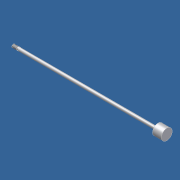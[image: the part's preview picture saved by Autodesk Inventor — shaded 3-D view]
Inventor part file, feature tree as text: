
AUTODESK INVENTOR PART (.ipt)
format: ipt  version: 2012 (Build 160160000, 160)  size: 136,192 bytes
history: native  units: in
note: dims shown in document units (in); Inventor stores cm internally (conversion verified against a paired STEP export)
features: other x112, sketch x3, revolve x2, thread x1, extrude x1
ambient origin geometry x8: Origin, YZ Plane, XZ Plane, XY Plane, X Axis, Y Axis, Z Axis, Center Point
bodies: Solid1 (feature_tree)
feature tree (119):
  revolve  "Revolution1"  Angle=360.0deg
  revolve  "Revolution2"  [1 undecoded]
  thread  "Thread1"  [1 undecoded]
  extrude  "Extrusion1"  [1 undecoded]
  other  "rod_cp_XY"
  other  "rod_cp_YZ"
  other  "rod_cp_ZX"
  other  "rod_cp_X"
  other  "rod_cp_Y"
  other  "rod_cp_Z"
  other  "rod_cp_Center"
  other  "to_rod_clevis_XY"
  other  "to_rod_clevis_YZ"
  other  "to_rod_clevis_ZX"
  other  "to_rod_clevis_X"
  other  "to_rod_clevis_Y"
  other  "to_rod_clevis_Z"
  other  "to_rod_clevis_Center"
  other  "rl2_XY"
  other  "rl2_YZ"
  other  "rl2_ZX"
  other  "rl2_X"
  other  "rl2_Y"
  other  "rl2_Z"
  other  "rl2_Center"
  other  "rl1_XY"
  other  "rl1_YZ"
  other  "rl1_ZX"
  other  "rl1_X"
  other  "rl1_Y"
  other  "rl1_Z"
  other  "rl1_Center"
  other  "thd1_XY"
  other  "thd1_YZ"
  other  "thd1_ZX"
  other  "thd1_X"
  other  "thd1_Y"
  other  "thd1_Z"
  other  "thd1_Center"
  other  "thd2_XY"
  other  "thd2_YZ"
  other  "thd2_ZX"
  other  "thd2_X"
  other  "thd2_Y"
  other  "thd2_Z"
  other  "thd2_Center"
  other  "dia1_XY"
  other  "dia1_YZ"
  other  "dia1_ZX"
  other  "dia1_X"
  other  "dia1_Y"
  other  "dia1_Z"
  other  "dia1_Center"
  other  "dia2_XY"
  other  "dia2_YZ"
  other  "dia2_ZX"
  other  "dia2_X"
  other  "dia2_Y"
  other  "dia2_Z"
  other  "dia2_Center"
  other  "wf1_XY"
  other  "wf1_YZ"
  other  "wf1_ZX"
  other  "wf1_X"
  other  "wf1_Y"
  other  "wf1_Z"
  other  "wf1_Center"
  other  "wf2_XY"
  other  "wf2_YZ"
  other  "wf2_ZX"
  other  "wf2_X"
  other  "wf2_Y"
  other  "wf2_Z"
  other  "wf2_Center"
  other  "hh1_XY"
  other  "hh1_YZ"
  other  "hh1_ZX"
  other  "hh1_X"
  other  "hh1_Y"
  other  "hh1_Z"
  other  "hh1_Center"
  other  "hh2_XY"
  other  "hh2_YZ"
  other  "hh2_ZX"
  other  "hh2_X"
  other  "hh2_Y"
  other  "hh2_Z"
  other  "hh2_Center"
  other  "dia12_XY"
  other  "dia12_YZ"
  other  "dia12_ZX"
  other  "dia12_X"
  other  "dia12_Y"
  other  "dia12_Z"
  other  "dia12_Center"
  other  "dia22_XY"
  other  "dia22_YZ"
  other  "dia22_ZX"
  other  "dia22_X"
  other  "dia22_Y"
  other  "dia22_Z"
  other  "dia22_Center"
  other  "wfw1_XY"
  other  "wfw1_YZ"
  other  "wfw1_ZX"
  other  "wfw1_X"
  other  "wfw1_Y"
  other  "wfw1_Z"
  other  "wfw1_Center"
  other  "wfw2_XY"
  other  "wfw2_YZ"
  other  "wfw2_ZX"
  other  "wfw2_X"
  other  "wfw2_Y"
  other  "wfw2_Z"
  other  "wfw2_Center"
  sketch  "Sketch_1"  dims[d0=360.0deg d1=360.0deg]
  sketch  "Sketch_3"  dims[d2=0.5in d3=0.0in d4=0.125in d5=0.0in]
  sketch  "Sketch_10"
note: 3 required parameter values undecoded (feature->parameter linkage not recoverable at this tier; creation-order binding heuristic only, values carry confidence <= 0.55)